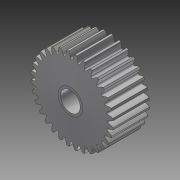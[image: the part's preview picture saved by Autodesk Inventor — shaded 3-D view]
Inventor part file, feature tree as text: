
AUTODESK INVENTOR PART (.ipt)
format: ipt  version: 2014 SP1 (Build 180222100, 222)  size: 671,744 bytes
history: native  units: in
note: dims shown in document units (in); Inventor stores cm internally (conversion verified against a paired STEP export)
features: mirror x1, other x1, imported_body x1
ambient origin geometry x8: Origin, YZ Plane, XZ Plane, XY Plane, X Axis, Y Axis, Z Axis, Center Point
bodies: Body1 (feature_tree)
feature tree (3):
  mirror  "Mirror1"
  other  "217-2625-005 Rev1_Planet_Revolving_Follower01.ipt1"
  imported_body  "Base1"
